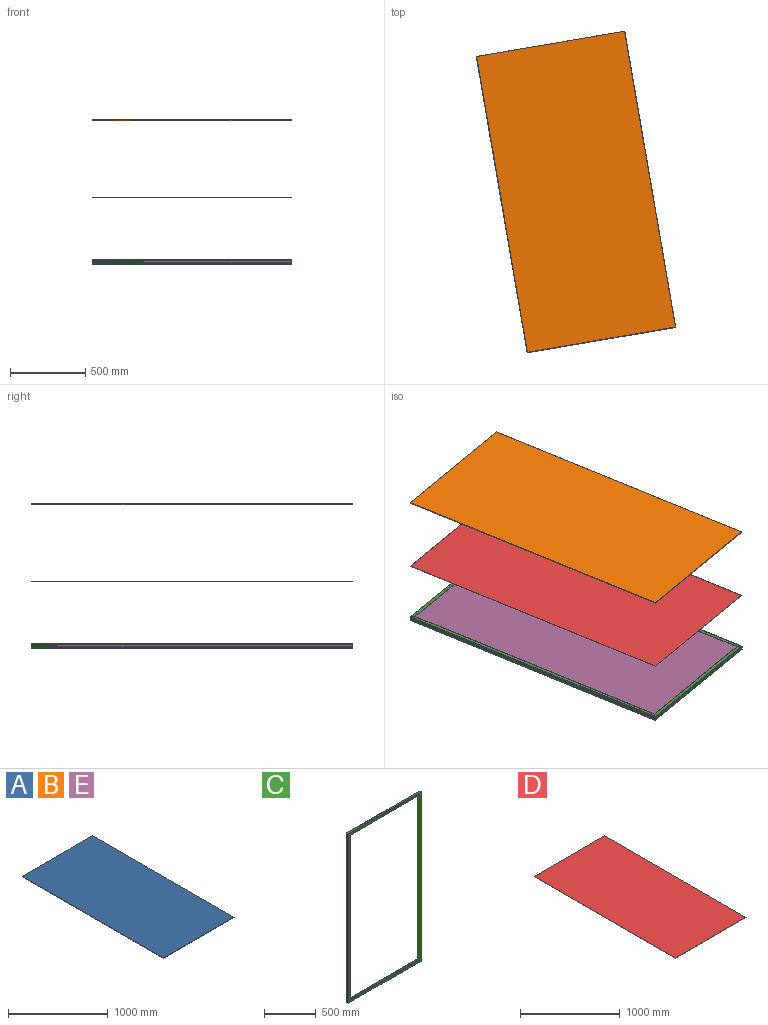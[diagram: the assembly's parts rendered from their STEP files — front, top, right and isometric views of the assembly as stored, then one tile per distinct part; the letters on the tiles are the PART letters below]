
ASSEMBLY  parts=5 mates=10
PART A: 6 faces, bbox 1000x2000x5 mm
  f0: plane 1000x5mm, normal (0,1,0), area 5000mm2, adj f1,f3,f4,f5
  f1: plane 2000x5mm, normal (-1,0,0), area 10000mm2, adj f0,f2,f4,f5
  f2: plane 1000x5mm, normal (0,-1,0), area 5000mm2, adj f1,f3,f4,f5
  f3: plane 2000x5mm, normal (1,0,0), area 10000mm2, adj f0,f2,f4,f5
  f4: plane 2000x1000mm, normal (0,0,1), area 2000000mm2, adj f0,f1,f2,f3
  f5: plane 2000x1000mm, normal (0,0,-1), area 2000000mm2, adj f0,f1,f2,f3
PART B: same geometry as A
PART C: 112 faces, bbox 1004x29x2004 mm
  f0: plane 2x0.01mm, normal (0,1,0), area 0mm2, adj f4,f5,f7,f28
  f1: plane 2x0.01mm, normal (0,-1,0), area 0mm2, adj f4,f5,f10,f20
  f2: plane 2x0.01mm, normal (0,1,0), area 0mm2, adj f4,f5,f11,f29
  f3: plane 2x0.01mm, normal (0,-1,0), area 0mm2, adj f4,f5,f6,f19
  f4: plane 995.4x20.4mm, normal (0,0,1), area 20306.2mm2, adj f0,f1,f2,f3,f8,f12,f21,f30
  f5: plane 995.4x20.4mm, normal (0,0,-1), area 20306.2mm2, adj f0,f1,f2,f3,f9,f13,f22,f31
  f6: plane 4.3x4.3mm, normal (0,-1,0), area 10.4mm2, adj f3,f8,f9,f89
  f7: plane 4.3x4.3mm, normal (0,1,0), area 10.4mm2, adj f0,f8,f9,f90
  f8: cylinder r=4.3mm len=20.4mm, axis (0,-1,0), area 137.8mm2, adj f4,f6,f7,f92
  f9: cylinder r=2.3mm len=20.4mm, axis (0,-1,0), area 73.7mm2, adj f5,f6,f7,f93
  f10: plane 4.3x4.3mm, normal (0,-1,0), area 10.4mm2, adj f1,f12,f13,f35
  f11: plane 4.3x4.3mm, normal (0,1,0), area 10.4mm2, adj f2,f12,f13,f32
  f12: cylinder r=4.3mm len=20.4mm, axis (0,-1,0), area 137.8mm2, adj f4,f10,f11,f36
  f13: cylinder r=2.3mm len=20.4mm, axis (0,-1,0), area 73.7mm2, adj f5,f10,f11,f37
  f14: plane 953.97x2mm, normal (0,0,-1), area 1907.9mm2, adj f15,f16,f17,f18
  f15: plane 20.7x20.7mm, normal (0.71,0,-0.71), area 58.5mm2, adj f14,f17,f18,f19
  f16: plane 20.7x20.7mm, normal (-0.71,0,-0.71), area 58.5mm2, adj f14,f17,f18,f20
  f17: plane 995.37x20.7mm, normal (0,-1,0), area 20175.7mm2, adj f14,f15,f16,f21
  f18: plane 995.37x20.7mm, normal (0,1,0), area 20175.7mm2, adj f14,f15,f16,f22
  f19: plane 4.3x4.3mm, normal (1,0,0), area 10.4mm2, adj f3,f15,f21,f22
  f20: plane 4.3x4.3mm, normal (-1,0,0), area 10.4mm2, adj f1,f16,f21,f22
  f21: cylinder r=4.3mm len=995.37mm, axis (1,0,0), area 6723.2mm2, adj f4,f17,f19,f20
  f22: cylinder r=2.3mm len=995.37mm, axis (1,0,0), area 3596.1mm2, adj f5,f18,f19,f20
  f23: plane 953.97x2mm, normal (0,0,-1), area 1907.9mm2, adj f24,f25,f26,f27
  f24: plane 20.7x20.7mm, normal (-0.71,0,-0.71), area 58.5mm2, adj f23,f26,f27,f29
  f25: plane 20.7x20.7mm, normal (0.71,0,-0.71), area 58.5mm2, adj f23,f26,f27,f28
  f26: plane 995.37x20.7mm, normal (0,1,0), area 20175.7mm2, adj f23,f24,f25,f30
  f27: plane 995.37x20.7mm, normal (0,-1,0), area 20175.7mm2, adj f23,f24,f25,f31
  f28: plane 4.3x4.3mm, normal (1,0,0), area 10.4mm2, adj f0,f25,f30,f31
  f29: plane 4.3x4.3mm, normal (-1,0,0), area 10.4mm2, adj f2,f24,f30,f31
  f30: cylinder r=4.3mm len=995.37mm, axis (1,0,0), area 6723.2mm2, adj f4,f26,f28,f29
  f31: cylinder r=2.3mm len=995.37mm, axis (1,0,0), area 3596.1mm2, adj f5,f27,f28,f29
  f32: plane 2x0.01mm, normal (0,1,0), area 0mm2, adj f11,f36,f37,f43
  f33: plane 2x0.01mm, normal (0,-1,0), area 0mm2, adj f36,f37,f38,f84
  f34: plane 2x0.01mm, normal (0,1,0), area 0mm2, adj f36,f37,f42,f85
  f35: plane 2x0.01mm, normal (0,-1,0), area 0mm2, adj f10,f36,f37,f39
  f36: plane 1995.4x20.4mm, normal (-1,0,0), area 40706.2mm2, adj f12,f32,f33,f34,f35,f40,f44,f86
  f37: plane 1995.4x20.4mm, normal (1,0,0), area 40706.2mm2, adj f13,f32,f33,f34,f35,f41,f45,f87
  f38: plane 4.3x4.3mm, normal (0,0,-1), area 10.4mm2, adj f33,f40,f41,f53
  f39: plane 4.3x4.3mm, normal (0,0,1), area 10.4mm2, adj f35,f40,f41,f52
  f40: cylinder r=4.3mm len=1995.37mm, axis (0,0,-1), area 13477.6mm2, adj f36,f38,f39,f54
  f41: cylinder r=2.3mm len=1995.37mm, axis (0,0,-1), area 7208.9mm2, adj f37,f38,f39,f55
  f42: plane 4.3x4.3mm, normal (0,0,-1), area 10.4mm2, adj f34,f44,f45,f47
  f43: plane 4.3x4.3mm, normal (0,0,1), area 10.4mm2, adj f32,f44,f45,f48
  f44: cylinder r=4.3mm len=1995.37mm, axis (0,0,-1), area 13477.6mm2, adj f36,f42,f43,f49
  f45: cylinder r=2.3mm len=1995.37mm, axis (0,0,-1), area 7208.9mm2, adj f37,f42,f43,f50
  f46: plane 1953.97x2mm, normal (1,0,0), area 3907.9mm2, adj f47,f48,f49,f50
  f47: plane 20.7x20.7mm, normal (0.71,0,-0.71), area 58.5mm2, adj f42,f46,f49,f50
  f48: plane 20.7x20.7mm, normal (0.71,0,0.71), area 58.5mm2, adj f43,f46,f49,f50
  f49: plane 1995.37x20.7mm, normal (0,1,0), area 40875.7mm2, adj f44,f46,f47,f48
  f50: plane 1995.37x20.7mm, normal (0,-1,0), area 40875.7mm2, adj f45,f46,f47,f48
  f51: plane 1953.97x2mm, normal (1,0,0), area 3907.9mm2, adj f52,f53,f54,f55
  f52: plane 20.7x20.7mm, normal (0.71,0,0.71), area 58.5mm2, adj f39,f51,f54,f55
  f53: plane 20.7x20.7mm, normal (0.71,0,-0.71), area 58.5mm2, adj f38,f51,f54,f55
  f54: plane 1995.37x20.7mm, normal (0,-1,0), area 40875.7mm2, adj f40,f51,f52,f53
  f55: plane 1995.37x20.7mm, normal (0,1,0), area 40875.7mm2, adj f41,f51,f52,f53
  f56: plane 4.3x4.3mm, normal (0,-1,0), area 10.4mm2, adj f58,f59,f60,f91
  f57: plane 4.3x4.3mm, normal (0,1,0), area 10.4mm2, adj f58,f59,f62,f88
  f58: cylinder r=4.3mm len=20.4mm, axis (0,-1,0), area 137.8mm2, adj f56,f57,f64,f92
  f59: cylinder r=2.3mm len=20.4mm, axis (0,-1,0), area 73.7mm2, adj f56,f57,f65,f93
  f60: plane 2x0.01mm, normal (0,-1,0), area 0mm2, adj f56,f64,f65,f75
  f61: plane 2x0.01mm, normal (0,1,0), area 0mm2, adj f64,f65,f67,f85
  f62: plane 2x0.01mm, normal (0,1,0), area 0mm2, adj f57,f64,f65,f66
  f63: plane 2x0.01mm, normal (0,-1,0), area 0mm2, adj f64,f65,f76,f84
  f64: plane 995.4x20.4mm, normal (0,0,-1), area 20306.2mm2, adj f58,f60,f61,f62,f63,f68,f77,f86
  f65: plane 995.4x20.4mm, normal (0,0,1), area 20306.2mm2, adj f59,f60,f61,f62,f63,f69,f78,f87
  f66: plane 4.3x4.3mm, normal (1,0,0), area 10.4mm2, adj f62,f68,f69,f71
  f67: plane 4.3x4.3mm, normal (-1,0,0), area 10.4mm2, adj f61,f68,f69,f72
  f68: cylinder r=4.3mm len=995.37mm, axis (1,0,0), area 6723.2mm2, adj f64,f66,f67,f73
  f69: cylinder r=2.3mm len=995.37mm, axis (1,0,0), area 3596.1mm2, adj f65,f66,f67,f74
  f70: plane 953.97x2mm, normal (0,0,1), area 1907.9mm2, adj f71,f72,f73,f74
  f71: plane 20.7x20.7mm, normal (0.71,0,0.71), area 58.5mm2, adj f66,f70,f73,f74
  f72: plane 20.7x20.7mm, normal (-0.71,0,0.71), area 58.5mm2, adj f67,f70,f73,f74
  f73: plane 995.37x20.7mm, normal (0,1,0), area 20175.7mm2, adj f68,f70,f71,f72
  f74: plane 995.37x20.7mm, normal (0,-1,0), area 20175.7mm2, adj f69,f70,f71,f72
  f75: plane 4.3x4.3mm, normal (1,0,0), area 10.4mm2, adj f60,f77,f78,f81
  f76: plane 4.3x4.3mm, normal (-1,0,0), area 10.4mm2, adj f63,f77,f78,f80
  f77: cylinder r=4.3mm len=995.37mm, axis (1,0,0), area 6723.2mm2, adj f64,f75,f76,f82
  f78: cylinder r=2.3mm len=995.37mm, axis (1,0,0), area 3596.1mm2, adj f65,f75,f76,f83
  f79: plane 953.97x2mm, normal (0,0,1), area 1907.9mm2, adj f80,f81,f82,f83
  f80: plane 20.7x20.7mm, normal (-0.71,0,0.71), area 58.5mm2, adj f76,f79,f82,f83
  f81: plane 20.7x20.7mm, normal (0.71,0,0.71), area 58.5mm2, adj f75,f79,f82,f83
  f82: plane 995.37x20.7mm, normal (0,-1,0), area 20175.7mm2, adj f77,f79,f80,f81
  f83: plane 995.37x20.7mm, normal (0,1,0), area 20175.7mm2, adj f78,f79,f80,f81
  f84: plane 4.3x4.3mm, normal (0,-1,0), area 10.4mm2, adj f33,f63,f86,f87
  f85: plane 4.3x4.3mm, normal (0,1,0), area 10.4mm2, adj f34,f61,f86,f87
  f86: cylinder r=4.3mm len=20.4mm, axis (0,-1,0), area 137.8mm2, adj f36,f64,f84,f85
  f87: cylinder r=2.3mm len=20.4mm, axis (0,-1,0), area 73.7mm2, adj f37,f65,f84,f85
  f88: plane 2x0.01mm, normal (0,1,0), area 0mm2, adj f57,f92,f93,f98
  f89: plane 2x0.01mm, normal (0,-1,0), area 0mm2, adj f6,f92,f93,f95
  f90: plane 2x0.01mm, normal (0,1,0), area 0mm2, adj f7,f92,f93,f99
  f91: plane 2x0.01mm, normal (0,-1,0), area 0mm2, adj f56,f92,f93,f94
  f92: plane 1995.4x20.4mm, normal (1,0,0), area 40706.2mm2, adj f8,f58,f88,f89,f90,f91,f96,f100
  f93: plane 1995.4x20.4mm, normal (-1,0,0), area 40706.2mm2, adj f9,f59,f88,f89,f90,f91,f97,f101
  f94: plane 4.3x4.3mm, normal (0,0,-1), area 10.4mm2, adj f91,f96,f97,f108
  f95: plane 4.3x4.3mm, normal (0,0,1), area 10.4mm2, adj f89,f96,f97,f109
  f96: cylinder r=4.3mm len=1995.37mm, axis (0,0,-1), area 13477.6mm2, adj f92,f94,f95,f110
  f97: cylinder r=2.3mm len=1995.37mm, axis (0,0,-1), area 7208.9mm2, adj f93,f94,f95,f111
  f98: plane 4.3x4.3mm, normal (0,0,-1), area 10.4mm2, adj f88,f100,f101,f104
  f99: plane 4.3x4.3mm, normal (0,0,1), area 10.4mm2, adj f90,f100,f101,f103
  f100: cylinder r=4.3mm len=1995.37mm, axis (0,0,-1), area 13477.6mm2, adj f92,f98,f99,f105
  f101: cylinder r=2.3mm len=1995.37mm, axis (0,0,-1), area 7208.9mm2, adj f93,f98,f99,f106
  f102: plane 1953.97x2mm, normal (-1,0,0), area 3907.9mm2, adj f103,f104,f105,f106
  f103: plane 20.7x20.7mm, normal (-0.71,0,0.71), area 58.5mm2, adj f99,f102,f105,f106
  f104: plane 20.7x20.7mm, normal (-0.71,0,-0.71), area 58.5mm2, adj f98,f102,f105,f106
  f105: plane 1995.37x20.7mm, normal (0,1,0), area 40875.7mm2, adj f100,f102,f103,f104
  f106: plane 1995.37x20.7mm, normal (0,-1,0), area 40875.7mm2, adj f101,f102,f103,f104
  f107: plane 1953.97x2mm, normal (-1,0,0), area 3907.9mm2, adj f108,f109,f110,f111
  f108: plane 20.7x20.7mm, normal (-0.71,0,-0.71), area 58.5mm2, adj f94,f107,f110,f111
  f109: plane 20.7x20.7mm, normal (-0.71,0,0.71), area 58.5mm2, adj f95,f107,f110,f111
  f110: plane 1995.37x20.7mm, normal (0,-1,0), area 40875.7mm2, adj f96,f107,f108,f109
  f111: plane 1995.37x20.7mm, normal (0,1,0), area 40875.7mm2, adj f97,f107,f108,f109
PART D: 6 faces, bbox 1000x2000x2 mm
  f0: plane 1000x2mm, normal (0,1,0), area 2000mm2, adj f1,f3,f4,f5
  f1: plane 2000x2mm, normal (-1,0,0), area 4000mm2, adj f0,f2,f4,f5
  f2: plane 1000x2mm, normal (0,-1,0), area 2000mm2, adj f1,f3,f4,f5
  f3: plane 2000x2mm, normal (1,0,0), area 4000mm2, adj f0,f2,f4,f5
  f4: plane 2000x1000mm, normal (0,0,1), area 2000000mm2, adj f0,f1,f2,f3
  f5: plane 2000x1000mm, normal (0,0,-1), area 2000000mm2, adj f0,f1,f2,f3
PART E: same geometry as A
PLACE A rot(axis=(0,0,1),9.8deg) t=(-23.58,-43.48,0)mm
PLACE B rot(axis=(0,0,1),9.8deg) t=(-23.58,-43.48,954.23)mm
PLACE C rot(axis=(0.99,0.08,0.08),90.4deg) t=(-23.58,-43.48,25)mm
PLACE D rot(axis=(0,0,1),9.8deg) t=(-23.58,-43.48,439.3)mm
PLACE E rot(axis=(0,0,1),9.8deg) t=(-23.58,-43.48,5)mm
MATE planar E.f5 <-> A.f4  axis (0,0,-1) through (-23.58,-43.48,5)mm
MATE planar E.f3 <-> C.f93  axis (0.99,0.17,0) through (469.19,41.23,7.5)mm
MATE planar C.f65 <-> E.f0  axis (0.17,-0.99,0) through (-193.01,942.06,12.5)mm
MATE planar C.f37 <-> B.f1  axis (0.99,0.17,0) through (-516.36,-128.19,12.5)mm
MATE planar B.f2 <-> C.f5  axis (0.17,-0.99,0) through (145.84,-1029.02,956.73)mm
MATE planar C.f5 <-> A.f2  axis (-0.17,0.99,0) through (145.84,-1029.02,12.5)mm
MATE planar A.f5 <-> C.f55  axis (0,0,-1) through (-516.36,-128.19,0)mm
MATE planar D.f2 <-> C.f5  axis (0.17,-0.99,0) through (145.84,-1029.02,440.3)mm
MATE planar C.f37 <-> A.f1  axis (0.99,0.17,0) through (-516.36,-128.19,12.5)mm
MATE planar C.f93 <-> D.f3  axis (-0.99,-0.17,0) through (469.19,41.23,12.5)mm
